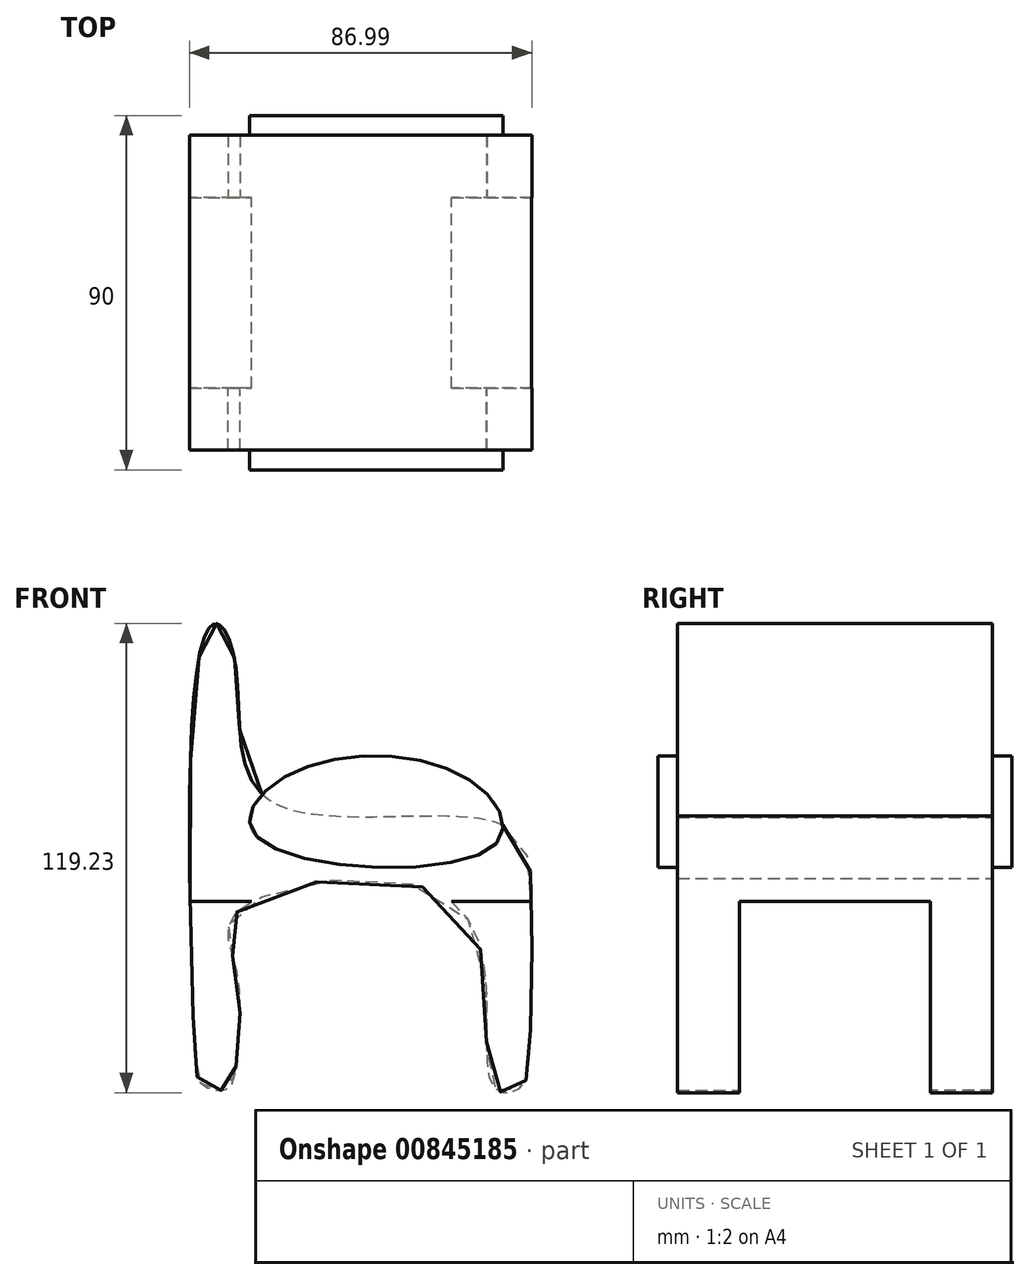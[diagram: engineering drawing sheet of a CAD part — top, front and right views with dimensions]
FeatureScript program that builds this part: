
annotation { "Feature Type Name" : "Feature", "Feature Type Description" : "" }
export const myFeature = defineFeature(function(context is Context, id is Id, definition is map)
    precondition{}
    {
        {
            var Q0;
            Q0=qCreatedBy(makeId("Front.planeOp"),FACE);
            var sketch = newSketch(context, id + "F0", { "sketchPlane" : qUnion([Q0])});
            skFitSpline(sketch, "E0", {"points": [v(-54.76, 45.8) * mm, v(-55.6, -50.8) * mm, v(-53.1, -60.8) * mm, v(-47.26, -61.63) * mm, v(-44.77, -54.14) * mm, v(-44.77, -31.65) * mm, v(-44.77, -16.66) * mm, v(11.87, -15.82) * mm, v(20.2, -60.8) * mm, v(26.86, -61.63) * mm, v(29.36, -55.8) * mm, v(30.2, -15.82) * mm, v(21.86, 5.83) * mm, v(-36.44, 11.66) * mm, v(-44.77, 44.14) * mm, v(-49.76, 56.63) * mm, v(-54.76, 45.8) * mm]});
            skSolve(sketch);
        }
        {
            var Q0;
            Q0 = qSketchRegion(id + "F0", true);
            extrude(context, id + "F1", {"entities" : qUnion([Q0]), "depth" : 80 * mm, "offsetDistance" : 25 * mm});
        }
        {
            var Q0;
            Q0=qCreatedBy(makeId("Right.planeOp"),FACE);
            var sketch = newSketch(context, id + "F2", { "sketchPlane" : qUnion([Q0])});
            skLineSegment(sketch, "E1.bottom", {"start": v(-64.22, -14.01) * mm, "end": v(-14.7, -14.01) * mm});
            skLineSegment(sketch, "E1.top", {"start": v(-64.22, -67.61) * mm, "end": v(-14.7, -67.61) * mm});
            skLineSegment(sketch, "E1.left", {"start": v(-64.22, -14.01) * mm, "end": v(-64.22, -67.61) * mm});
            skLineSegment(sketch, "E1.right", {"start": v(-14.7, -14.01) * mm, "end": v(-14.7, -67.61) * mm});
            skSolve(sketch);
        }
        {
            var Q0;
            Q0 = qSketchRegion(id + "F2", true);
            extrude(context, id + "F3", {"entities" : qUnion([Q0]), "operationType" : NewBodyOperationType.REMOVE, "endBound" : BoundingType.THROUGH_ALL, "depth" : 25 * mm, "offsetDistance" : 25 * mm, "hasSecondDirection" : true, "secondDirectionOppositeDirection" : true, "secondDirectionDepth" : 60 * mm});
        }
        {
            var Q0;
            Q0=qCreatedBy(makeId("Front.planeOp"),FACE);
            cPlane(context, id + "F4", {"entities" : qUnion([Q0]), "cplaneType" : CPlaneType.OFFSET, "offset" : 80 * mm, "width" : 150 * mm, "height" : 150 * mm});
        }
        {
            var Q0;
            Q0=qCreatedBy(id+"F4.planeOp",FACE);
            var sketch = newSketch(context, id + "F5", { "sketchPlane" : qUnion([Q0])});
            skFitSpline(sketch, "E2", {"points": [v(-39.63, 2.41) * mm, v(-31.2, 18.41) * mm, v(14.44, 16.9) * mm, v(20.34, 0) * mm, v(-39.63, 2.41) * mm]});
            skSolve(sketch);
        }
        {
            var Q0;
            Q0 = qSketchRegion(id + "F5", true);
            extrude(context, id + "F6", {"entities" : qUnion([Q0]), "operationType" : NewBodyOperationType.ADD, "depth" : 5 * mm, "offsetDistance" : 25 * mm});
        }
        {
            var Q0;
            Q0=qCreatedBy(makeId("Front.planeOp"),FACE);
            cPlane(context, id + "F7", {"entities" : qUnion([Q0]), "cplaneType" : CPlaneType.OFFSET, "offset" : 40 * mm, "width" : 150 * mm, "height" : 150 * mm});
        }
        {
            var Q0;
            Q0=makeQuery(id+"F1.opExtrude","SWEPT_BODY",BODY,{"disambiguationData":[OSD([sQuery(id+"F0.wireOp",EDGE,"E0")])]});
            var Q1;
            Q1=qCreatedBy(id+"F7.planeOp",FACE);
            mirror(context, id + "F8", {"operationType" : NewBodyOperationType.ADD, "entities" : qUnion([Q0]), "mirrorPlane" : qUnion([Q1])});
        }
    });
